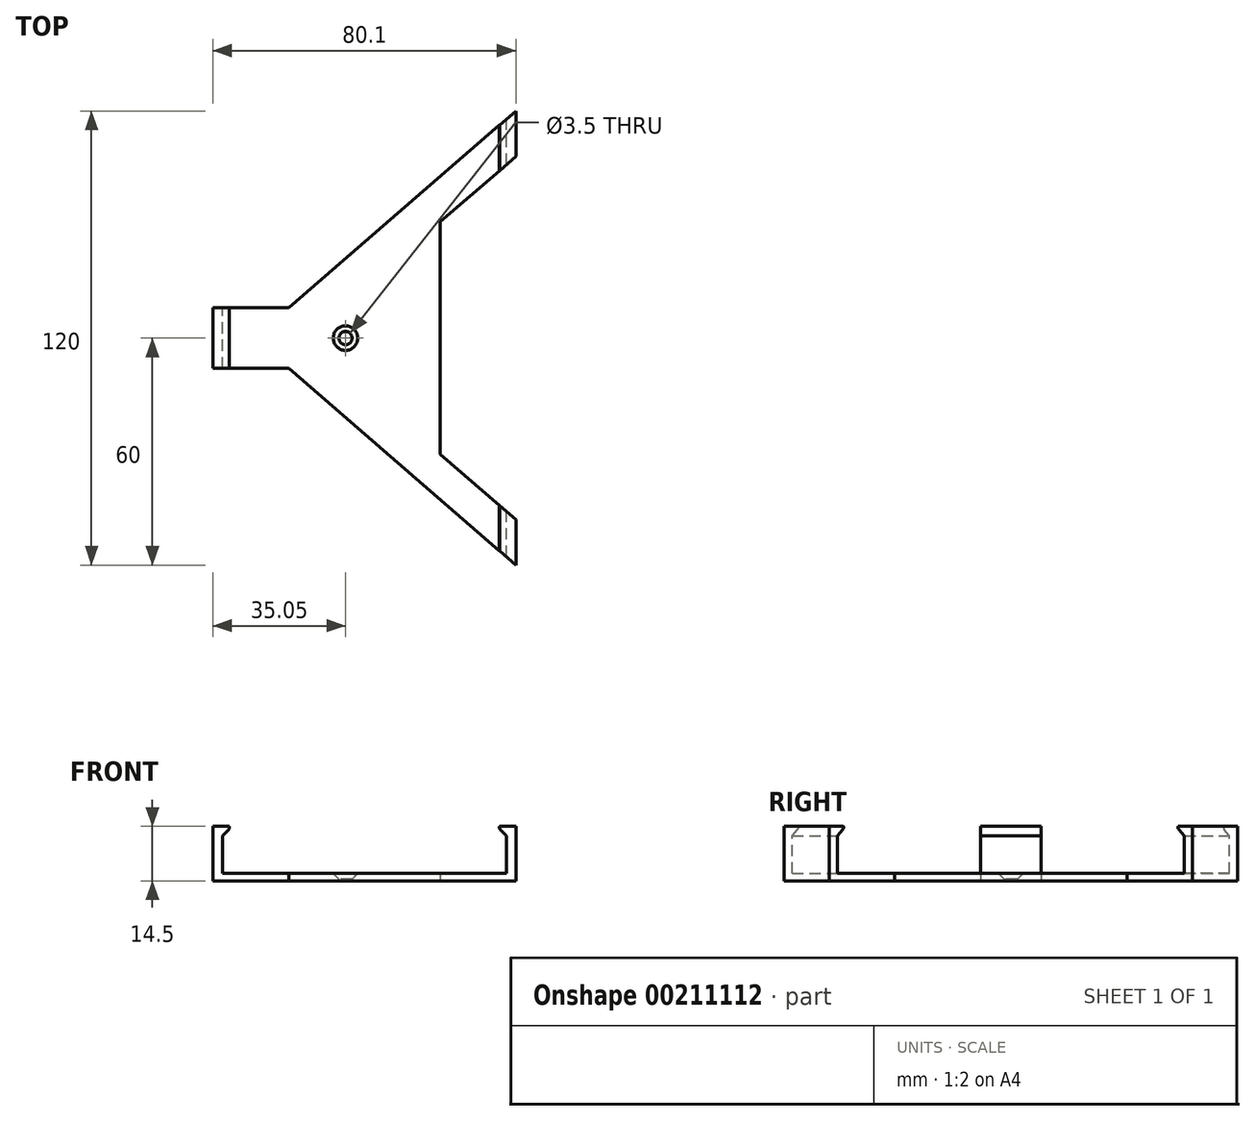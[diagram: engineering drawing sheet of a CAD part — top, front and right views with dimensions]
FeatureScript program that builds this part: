
annotation { "Feature Type Name" : "Feature", "Feature Type Description" : "" }
export const myFeature = defineFeature(function(context is Context, id is Id, definition is map)
    precondition{}
    {
        {
            var Q0;
            Q0=qCreatedBy(makeId("Front.planeOp"),FACE);
            var sketch = newSketch(context, id + "F0", { "sketchPlane" : qUnion([Q0])});
            skLineSegment(sketch, "E0", {"start": v(0, 0) * mm, "end": v(-37.55, 0) * mm});
            skLineSegment(sketch, "E1", {"start": v(-37.55, 0) * mm, "end": v(-37.55, 10) * mm});
            skLineSegment(sketch, "E2.0", {"start": v(-40.05, 13) * mm, "end": v(-34.55, 13) * mm});
            skLineSegment(sketch, "E2.1", {"start": v(-40.05, -2) * mm, "end": v(-40.05, 13) * mm});
            skLineSegment(sketch, "E2.2", {"start": v(0, -2) * mm, "end": v(-40.05, -2) * mm});
            skLineSegment(sketch, "E3", {"start": v(-37.55, 10) * mm, "end": v(-34.55, 13) * mm});
            skLineSegment(sketch, "E4.MirrorCS", {"start": v(40.05, -2) * mm, "end": v(40.05, 13) * mm});
            skLineSegment(sketch, "E5.MirrorCS", {"start": v(0, -2) * mm, "end": v(40.05, -2) * mm});
            skLineSegment(sketch, "E6.MirrorCS", {"start": v(37.55, 0) * mm, "end": v(37.55, 10) * mm});
            skLineSegment(sketch, "E7.MirrorCS", {"start": v(40.05, 13) * mm, "end": v(34.55, 13) * mm});
            skLineSegment(sketch, "E8.MirrorCS", {"start": v(0, 0) * mm, "end": v(37.55, 0) * mm});
            skLineSegment(sketch, "E9.MirrorCS", {"start": v(37.55, 10) * mm, "end": v(34.55, 13) * mm});
            skSolve(sketch);
        }
        {
            var Q0;
            Q0 = qSketchRegion(id + "F0", true);
            extrude(context, id + "F1", {"entities" : qUnion([Q0]), "endBound" : BoundingType.SYMMETRIC, "depth" : 120 * mm});
        }
        {
            var Q0;
            Q0=makeQuery(id+"F1.opExtrude","SWEPT_EDGE",EDGE,{"disambiguationData":[OSD([sQuery(id+"F0.wireOp",EDGE,"E2.0"),sQuery(id+"F0.wireOp",EDGE,"E3")])]});
            var Q1;
            Q1=makeQuery(id+"F1.opExtrude","SWEPT_EDGE",EDGE,{"disambiguationData":[OSD([sQuery(id+"F0.wireOp",EDGE,"E7.MirrorCS"),sQuery(id+"F0.wireOp",EDGE,"E9.MirrorCS")])]});
            fillet(context, id + "F2", {"entities" : qUnion([Q0, Q1]), "radius" : .8 * mm, "tangentPropagation" : true, "allowEdgeOverflow" : false});
        }
        {
            var Q0;
            Q0=makeQuery(id+"F1.opExtrude","SWEPT_FACE",FACE,{"disambiguationData":[OSD([sQuery(id+"F0.wireOp",EDGE,"E0"),sQuery(id+"F0.wireOp",EDGE,"E8.MirrorCS")])]});
            var sketch = newSketch(context, id + "F3", { "sketchPlane" : qUnion([Q0])});
            skLineSegment(sketch, "E10", {"start": v(40.05, -60) * mm, "end": v(40.05, -48) * mm});
            skLineSegment(sketch, "E11", {"start": v(40.05, -48) * mm, "end": v(20.05, -30.7) * mm});
            skLineSegment(sketch, "E12", {"start": v(20.05, -30.7) * mm, "end": v(20.05, 0) * mm});
            skLineSegment(sketch, "E13", {"start": v(40.05, -60) * mm, "end": v(-20.05, -8) * mm});
            skLineSegment(sketch, "E14", {"start": v(-20.05, -8) * mm, "end": v(-40.05, -8) * mm});
            skLineSegment(sketch, "E15", {"start": v(-40.05, -8) * mm, "end": v(-40.05, 0) * mm});
            skLineSegment(sketch, "E16.MirrorCS", {"start": v(20.05, 30.7) * mm, "end": v(20.05, 0) * mm});
            skLineSegment(sketch, "E17.MirrorCS", {"start": v(-20.05, 8) * mm, "end": v(-40.05, 8) * mm});
            skLineSegment(sketch, "E18.MirrorCS", {"start": v(-40.05, 8) * mm, "end": v(-40.05, 0) * mm});
            skLineSegment(sketch, "E19.MirrorCS", {"start": v(40.05, 60) * mm, "end": v(40.05, 48) * mm});
            skLineSegment(sketch, "E20.MirrorCS", {"start": v(40.05, 60) * mm, "end": v(-20.05, 8) * mm});
            skLineSegment(sketch, "E21.MirrorCS", {"start": v(40.05, 48) * mm, "end": v(20.05, 30.7) * mm});
            skSolve(sketch);
        }
        {
            var Q0;
            Q0 = qSketchRegion(id + "F3", true);
            extrude(context, id + "F4", {"entities" : qUnion([Q0]), "operationType" : NewBodyOperationType.INTERSECT, "endBound" : BoundingType.SYMMETRIC, "depth" : 25 * mm});
        }
        {
            var Q0;
            Q0=makeQuery(id+"F1.opExtrude","SWEPT_FACE",FACE,{"disambiguationData":[OSD([sQuery(id+"F0.wireOp",EDGE,"E0"),sQuery(id+"F0.wireOp",EDGE,"E8.MirrorCS")])]});
            var sketch = newSketch(context, id + "F5", { "sketchPlane" : qUnion([Q0])});
            skPoint(sketch, "E22", {"position": v(-5, 0) * mm});
            skSolve(sketch);
        }
        {
            var Q0;
            Q0=sQuery(id+"F5.wireOp",VERTEX,"E22");
            var Q1;
            Q1=makeQuery(id+"F1.opExtrude","SWEPT_BODY",BODY,{"disambiguationData":[OSD([sQuery(id+"F0.wireOp",EDGE,"E0"),sQuery(id+"F0.wireOp",EDGE,"E1"),sQuery(id+"F0.wireOp",EDGE,"E2.0"),sQuery(id+"F0.wireOp",EDGE,"E2.1"),sQuery(id+"F0.wireOp",EDGE,"E2.2"),sQuery(id+"F0.wireOp",EDGE,"E3"),sQuery(id+"F0.wireOp",EDGE,"E4.MirrorCS"),sQuery(id+"F0.wireOp",EDGE,"E5.MirrorCS"),sQuery(id+"F0.wireOp",EDGE,"E6.MirrorCS"),sQuery(id+"F0.wireOp",EDGE,"E7.MirrorCS"),sQuery(id+"F0.wireOp",EDGE,"E8.MirrorCS"),sQuery(id+"F0.wireOp",EDGE,"E9.MirrorCS")])]});
            hole(context, id + "F6", {"style" : HoleStyle.C_SINK, "endStyle" : HoleEndStyle.THROUGH, "holeDiameter" : 3.5 * mm, "cSinkDiameter" : 6.5 * mm, "cSinkAngle" : 90 * degree, "tappedDepth" : 12 * mm, "tapClearance" : 3, "locations" : qUnion([Q0]), "scope" : qUnion([Q1])});
        }
    });
